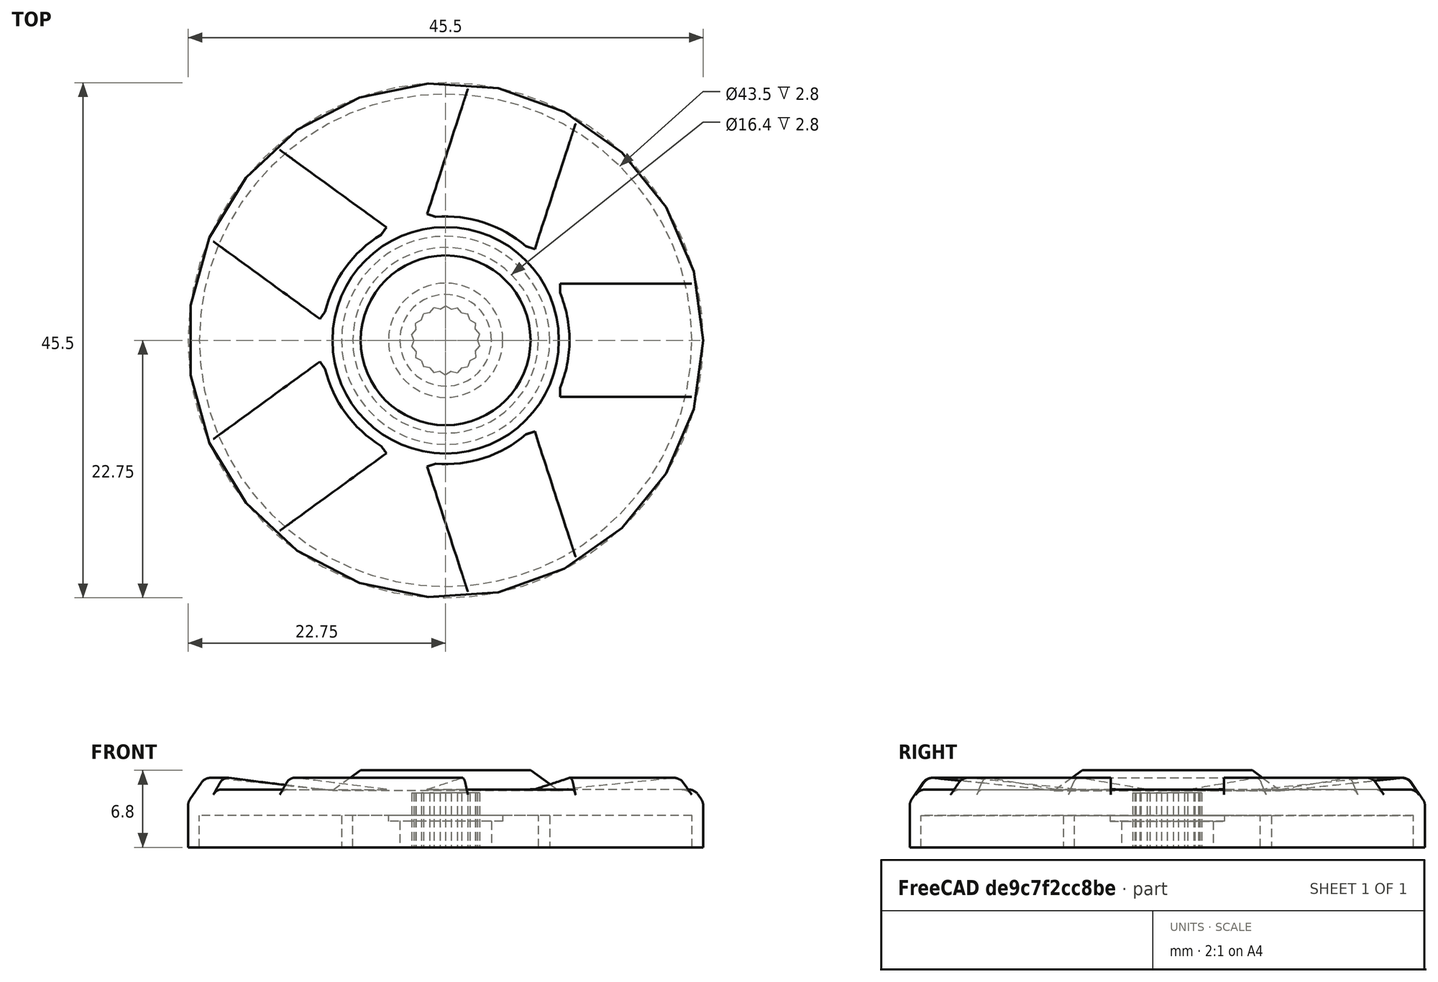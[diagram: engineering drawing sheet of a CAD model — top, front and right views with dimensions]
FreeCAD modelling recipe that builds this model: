
FCSTD DOCUMENT  (FreeCAD 1.1R20260325 (Git shallow))
Label: Sena20S
License: All rights reserved
LicenseURL: http://en.wikipedia.org/wiki/All_rights_reserved
objects: Sketcher::SketchObject×3, App::Point×2, PartDesign::Pocket×2, PartDesign::PolarPattern×2, PartDesign::Revolution×1, Spreadsheet::Sheet×1, PartDesign::Fillet×1, PartDesign::Body×1, App::Part×1, Mesh::Feature×1
note: 23 computed .brp shape members not serialized (recipe doc carries the construction recipe); baked Part::Feature solids carry a one-line shape summary decoded from their .brp

FEATURE [App::Point] Origin001
  Role = Origin
FEATURE [App::Point] Origin003
  Role = Origin
FEATURE [Sketcher::SketchObject] Sketch  label="Sketch-Body"
  ArcFitTolerance = 1e-06
  AttachmentSupport = -> [Origin002]
  ExternalTypes = [0]
  FullyConstrained = true
  MakeInternals = false
  MapMode = 5
  Placement = pos=(0,0,0) rot=(1,0,0;1.5708rad)
  _ExternalGeoVersion = 1
  expr: Constraints[25] = 15 / 2
  expr: Constraints[26] = 20 / 2
  expr: Constraints[41] = 45.5 / 2
  expr: Constraints[48] = Spreadsheet.Max / 2 + 1
  sketch-geometry (17):
    g0: LineSegment StartX=0 StartY=4 StartZ=0 EndX=7.5 EndY=4 EndZ=0
    g1: LineSegment StartX=7.5 StartY=4 StartZ=0 EndX=10 EndY=2.2 EndZ=0
    g2: LineSegment StartX=10 StartY=2.2 StartZ=0 EndX=21.25 EndY=3.4 EndZ=0
    g3: LineSegment StartX=21.25 StartY=3.4 StartZ=0 EndX=22.75 EndY=1.2 EndZ=0
    g4: LineSegment StartX=22.75 StartY=1.2 StartZ=0 EndX=22.75 EndY=-2.8 EndZ=0
    g5: LineSegment StartX=22.75 StartY=-2.8 StartZ=0 EndX=21.75 EndY=-2.8 EndZ=0
    g6: LineSegment StartX=21.75 StartY=-2.8 StartZ=0 EndX=21.75 EndY=0 EndZ=0
    g7: LineSegment StartX=21.75 StartY=0 StartZ=0 EndX=9.2 EndY=0 EndZ=0
    g8: LineSegment StartX=9.2 StartY=0 StartZ=0 EndX=9.2 EndY=-2.8 EndZ=0
    g9: LineSegment StartX=8.2 StartY=-2.8 StartZ=0 EndX=8.2 EndY=0 EndZ=0
    g10: LineSegment StartX=8.2 StartY=0 StartZ=0 EndX=5.05 EndY=0 EndZ=0
    g11: LineSegment StartX=5.05 StartY=0 StartZ=0 EndX=5.05 EndY=-0.5 EndZ=0
    g12: LineSegment StartX=5.05 StartY=-0.5 StartZ=0 EndX=4.05 EndY=-0.5 EndZ=0
    g13: LineSegment StartX=4.05 StartY=-0.5 StartZ=0 EndX=4.05 EndY=-2.8 EndZ=0
    g14: LineSegment StartX=4.05 StartY=-2.8 StartZ=0 EndX=0 EndY=-2.8 EndZ=0
    g15: LineSegment StartX=8.2 StartY=-2.8 StartZ=0 EndX=9.2 EndY=-2.8 EndZ=0
    g16: LineSegment StartX=0 StartY=4 StartZ=0 EndX=0 EndY=-2.8 EndZ=0
  constraints (49):
    c: PointOnObject(g0,g-2)
    c: Horizontal(g0)
    c: Coincident(g1,g0)
    c: Coincident(g2,g1)
    c: Coincident(g3,g2)
    c: Coincident(g4,g3)
    c: Vertical(g4)
    c: Coincident(g5,g4)
    c: Horizontal(g5)
    c: Coincident(g6,g5)
    c: Vertical(g6)
    c: Coincident(g7,g6)
    c: Vertical(g8)
    c: Vertical(g9)
    c: Coincident(g11,g10)
    c: Vertical(g11)
    c: Horizontal(g12)
    c: Vertical(g13)
    c: Horizontal(g14)
    c: Coincident(g8,g7)
    c: Coincident(g12,g11)
    c: Coincident(g13,g12)
    c: Coincident(g14,g13)
    c: Coincident(g10,g9)
    c: DistanceX(g5,g5) = 1
    c: DistanceX(g0,g0) = 7.5
    c: DistanceX(g0,g1) = 10
    c: DistanceY(g1,g0) = 1.8
    c: DistanceX(g12,g12) = 1
    c: DistanceY(g4,g4) = 4
    c: DistanceY(g3,g2) = 2.2
    c: Coincident(g15,g9)
    c: Coincident(g15,g8)
    c: Horizontal(g15)
    c: DistanceX(g15,g15) = 1
    c: Tangent(g7,g-1)
    c: Tangent(g10,g-1)
    c: DistanceY(g6,g6) = 2.8
    c: DistanceY(g-1,g0) = 4
    c: DistanceY(g8,g8) = 2.8
    c: DistanceX(g2,g3) = 1.5
    c: DistanceX(g-1,g4) = 22.75
    c: DistanceX(g-1,g9) = 8.2
    c: DistanceY(g11,g11) = 0.5
    c: Coincident(g16,g0)
    c: PointOnObject(g16,g-2)
    c: Coincident(g16,g14)
    c: DistanceY(g14,g-1) = 2.8
    c: DistanceX(g14,g13) = 4.05
FEATURE [PartDesign::Revolution] Revolution
  Angle = 360
  Angle2 = 0
  Axis = (0,2e-16,1)
  Base = (0,0,0)
  FuseOrder = 0
  Profile = -> Sketch
  ReferenceAxis = -> Sketch [V_Axis]
  Reversed = true
  Suppressed = false
  Type = 0
FEATURE [Spreadsheet::Sheet] Spreadsheet
  cells = A3='Spline; B3(Spline)=18; A4='Min; B4(Min)=5.6; D4=5.52; E4='measured; A5='Max; B5(Max)=6.1; D5=5.9; E5='measured; A6='Angle; B6(Angle)==360 / B3; C6='calc
FEATURE [Sketcher::SketchObject] Sketch001  label="Sketch-Spline"
  ArcFitTolerance = 1e-06
  AttachmentOffset = pos=(0,0,2) rot=(0,0,1;0rad)
  AttachmentSupport = -> [Origin002]
  ExternalTypes = [0]
  FullyConstrained = true
  MakeInternals = false
  MapMode = 5
  Placement = pos=(0,0,2) rot=(0,0,1;0rad)
  _ExternalGeoVersion = 1
  expr: Constraints[10] = Spreadsheet.Angle
  expr: Constraints[2] = Spreadsheet.Min / 2
  expr: Constraints[3] = Spreadsheet.Min / 2
  expr: Constraints[4] = Spreadsheet.Max / 2
  sketch-geometry (4):
    g0: LineSegment StartX=0 StartY=3.05 StartZ=0 EndX=-0.486215 EndY=2.75746 EndZ=0
    g1: LineSegment StartX=0 StartY=3.05 StartZ=0 EndX=0.486215 EndY=2.75746 EndZ=0
    g2: LineSegment StartX=-0.486215 StartY=2.75746 StartZ=0 EndX=0 EndY=0 EndZ=0
    g3: LineSegment StartX=0.486215 StartY=2.75746 StartZ=0 EndX=0 EndY=0 EndZ=0
  constraints (11):
    c: PointOnObject(g0,g-2)
    c: Coincident(g1,g0)
    c: Distance(g-1,g0) = 2.8
    c: Distance(g-1,g1) = 2.8
    c: Distance(g-1,g0) = 3.05
    c: Coincident(g2,g0)
    c: Coincident(g2,g-1)
    c: Coincident(g3,g1)
    c: Coincident(g3,g2)
    c: Equal(g0,g1)
    c: Angle(g3,g2) = 0.349066
FEATURE [PartDesign::Pocket] Pocket  label="Pocket-Spline"
  BaseFeature = -> Revolution
  Direction = (0,0,-1)
  Length = 10
  Length2 = 5
  Profile = -> Sketch001
  ReferenceAxis = -> Sketch001 [N_Axis]
  SideType = 0
  Suppressed = false
  Type = 0
  Type2 = 0
FEATURE [PartDesign::PolarPattern] PolarPattern
  Angle = 360
  Axis = -> Sketch001 [N_Axis]
  BaseFeature = -> Pocket
  Mode = 0
  Occurrences = 18
  Offset = 120
  Originals = -> [Pocket]
  SpacingPattern = [0]
  Spacings = [-1,-1,-1,-1,-1,-1,-1,-1,-1,-1,-1,-1,-1,-1,-1,-1,-1]
  Suppressed = false
  TransformMode = 0
  expr: Occurrences = Spreadsheet.Spline
FEATURE [Sketcher::SketchObject] Sketch002  label="Sketch-Cuts"
  ArcFitTolerance = 1e-06
  AttachmentSupport = -> [Origin002]
  ExternalTypes = [0]
  FullyConstrained = true
  MakeInternals = false
  MapMode = 5
  Placement = pos=(0,0,0) rot=(1,0,0;1.5708rad)
  _ExternalGeoVersion = 1
  sketch-geometry (4):
    g0: LineSegment StartX=10.1 StartY=4.3 StartZ=0 EndX=22.1 EndY=4.3 EndZ=0
    g1: LineSegment StartX=22.1 StartY=4.3 StartZ=0 EndX=22.1 EndY=2.3 EndZ=0
    g2: LineSegment StartX=22.1 StartY=2.3 StartZ=0 EndX=10.1 EndY=2.3 EndZ=0
    g3: LineSegment StartX=10.1 StartY=2.3 StartZ=0 EndX=10.1 EndY=4.3 EndZ=0
  constraints (12):
    c: Coincident(g1,g0)
    c: Vertical(g1)
    c: Coincident(g3,g2)
    c: Coincident(g3,g0)
    c: Coincident(g2,g1)
    c: Parallel(g3,g1)
    c: Parallel(g2,g0)
    c: DistanceY(g3,g3) = 2
    c: DistanceX(g0,g0) = 12
    c: DistanceX(g-1,g2) = 10.1
    c: DistanceY(g-1,g2) = 2.3
    c: Parallel(g2,g-1)
FEATURE [PartDesign::Pocket] Pocket001  label="Pocket-Cuts"
  BaseFeature = -> PolarPattern
  Direction = (0,1,-2e-16)
  Length = 10
  Length2 = 5
  Profile = -> Sketch002
  ReferenceAxis = -> Sketch002 [N_Axis]
  SideType = 2
  Suppressed = false
  Type = 0
  Type2 = 0
FEATURE [PartDesign::PolarPattern] PolarPattern001  label="PolarPattern-Cuts"
  Angle = 360
  Axis = -> Z_Axis001
  BaseFeature = -> Pocket001
  Mode = 0
  Occurrences = 5
  Offset = 120
  Originals = -> [Pocket001]
  SpacingPattern = [0]
  Spacings = [-1,-1,-1,-1]
  Suppressed = false
  TransformMode = 0
FEATURE [PartDesign::Fillet] Fillet
  Base = -> PolarPattern001 [Edge45,Edge14,Edge20,Edge26,Edge32,Edge8,Edge57,Edge40,Edge41,Edge48,Edge51,Edge54]
  BaseFeature = -> PolarPattern001
  Radius = 1
  SupportTransform = false
  Suppressed = false
  UseAllEdges = false
FEATURE [PartDesign::Body] Body
  AllowCompound = true
  Group = -> [Sketch,Revolution,Sketch001,Pocket,PolarPattern,Sketch002,Pocket001,PolarPattern001,Fillet]
  Origin = -> Origin002
  Tip = -> Fillet
FEATURE [App::Part] Part
  Group = -> [Body]
  Origin = -> Origin
FEATURE [Mesh::Feature] Mesh  label="Fillet (Meshed)"
